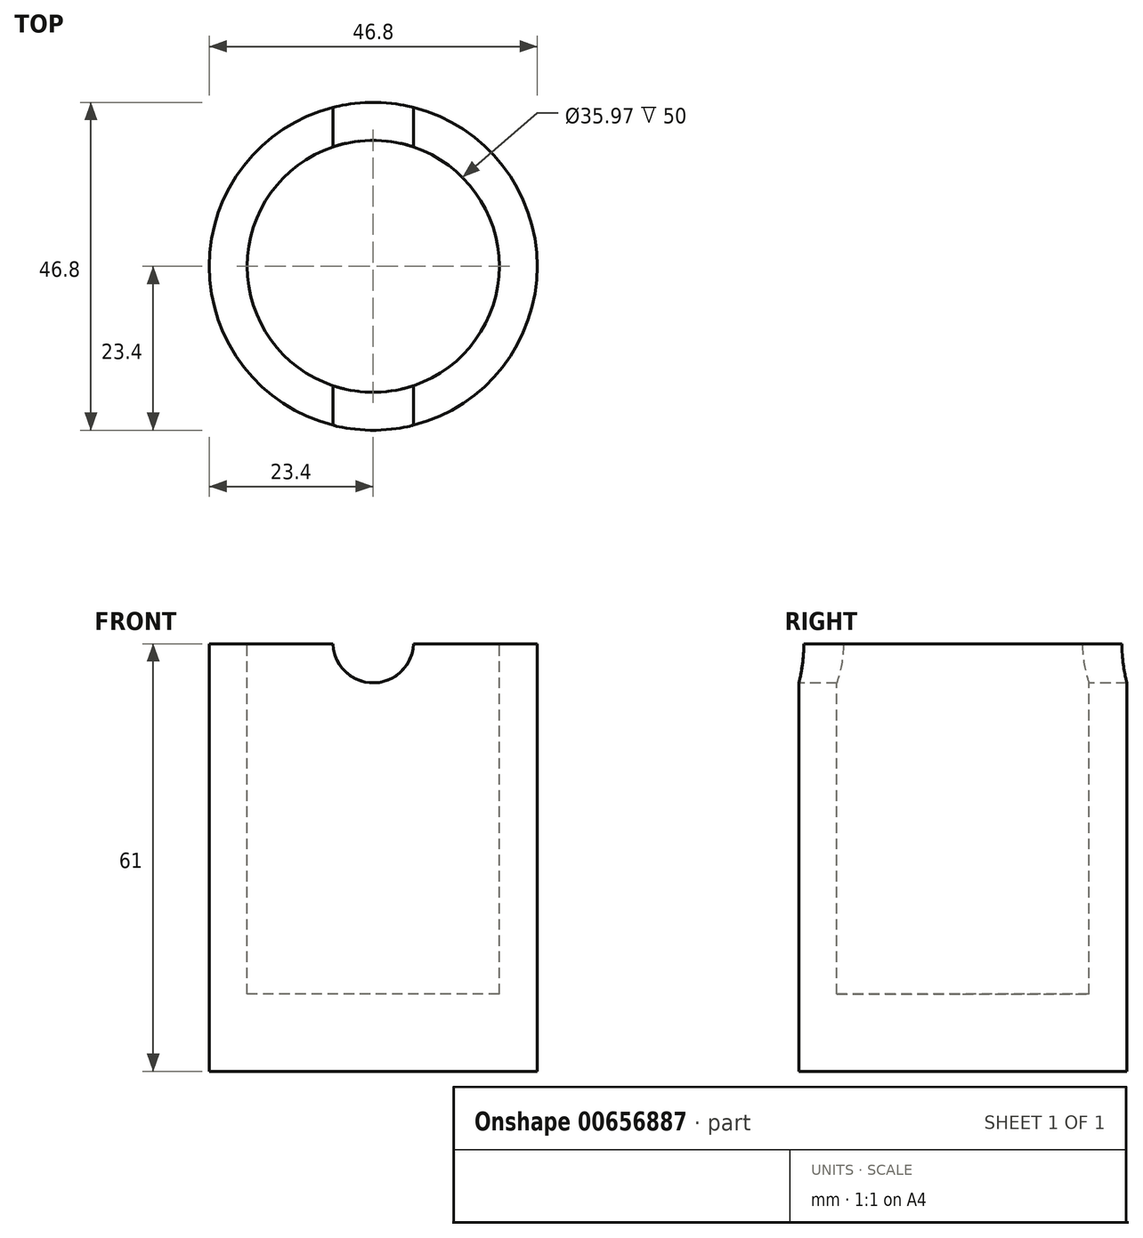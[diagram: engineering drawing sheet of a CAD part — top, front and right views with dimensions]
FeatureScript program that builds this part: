
annotation { "Feature Type Name" : "Feature", "Feature Type Description" : "" }
export const myFeature = defineFeature(function(context is Context, id is Id, definition is map)
    precondition{}
    {
        {
            var Q0;
            Q0=qCreatedBy(makeId("Top.planeOp"),FACE);
            var sketch = newSketch(context, id + "F0", { "sketchPlane" : qUnion([Q0])});
            skCircle(sketch, "E0", {"center": v(0, 0) * mm, "radius": 23.4 * mm});
            skSolve(sketch);
        }
        {
            var Q0;
            Q0 = qSketchRegion(id + "F0", true);
            extrude(context, id + "F1", {"entities" : qUnion([Q0]), "depth" : 61 * mm, "offsetDistance" : 25 * mm});
        }
        {
            var Q0;
            Q0=makeQuery(id+"F1.opExtrude","CAP_FACE",FACE,{"disambiguationData":[OSD([sQuery(id+"F0.wireOp",EDGE,"E0")])],"isStart":false});
            cPlane(context, id + "F2", {"entities" : qUnion([Q0]), "cplaneType" : CPlaneType.OFFSET, "offset" : 0 * mm, "width" : 150 * mm, "height" : 150 * mm});
        }
        {
            var Q0;
            Q0=qCreatedBy(id+"F2.planeOp",FACE);
            var sketch = newSketch(context, id + "F3", { "sketchPlane" : qUnion([Q0])});
            skCircle(sketch, "E1", {"center": v(0, 0) * mm, "radius": 17.98 * mm});
            skSolve(sketch);
        }
        {
            var Q0;
            Q0=makeQuery(id+"F3.imprint","IMPRINT",FACE,{"disambiguationData":[TD([[makeQuery(id+"F3.imprint","IMPRINT",EDGE,{"derivedFrom":sQuery(id+"F3.wireOp",EDGE,"E1")}),1.0]])]});
            extrude(context, id + "F4", {"entities" : qUnion([Q0]), "operationType" : NewBodyOperationType.REMOVE, "oppositeDirection" : true, "depth" : 50 * mm, "offsetDistance" : 25 * mm});
        }
        {
            var Q0;
            Q0=qCreatedBy(makeId("Front.planeOp"),FACE);
            cPlane(context, id + "F5", {"entities" : qUnion([Q0]), "cplaneType" : CPlaneType.OFFSET, "offset" : 25 * mm, "width" : 150 * mm, "height" : 150 * mm});
        }
        {
            var Q0;
            Q0=qCreatedBy(id+"F5.planeOp",FACE);
            var sketch = newSketch(context, id + "F6", { "sketchPlane" : qUnion([Q0])});
            skCircle(sketch, "E2", {"center": v(0, 61.19) * mm, "radius": 5.74 * mm});
            skSolve(sketch);
        }
        {
            var Q0;
            Q0 = qSketchRegion(id + "F6", true);
            extrude(context, id + "F7", {"entities" : qUnion([Q0]), "operationType" : NewBodyOperationType.REMOVE, "oppositeDirection" : true, "depth" : 63.5 * mm, "offsetDistance" : 25 * mm});
        }
    });
